# Revit family: Toilet_Elongated-American_Standard-Studio_S-2548A100.020
name_source: partatom
category: Plumbing Fixtures
units: mm (PartAtom-declared; Revit-internal decimal feet)

## family parameters
Always vertical = No
Cut with Voids When Loaded = No
OmniClass Number = 23.45.05.21.11
OmniClass Title = Water Closets
Part Type = Normal
Room Calculation Point = No
Round Connector Dimension = Use Diameter
Shared = Yes
Work Plane-Based = Yes

## types (1)
- 2548A100.020
    ADA Compliant = Yes
    Assembly Code = D2010110
    Bowl Shape = Elongated
    CEC Compliant = Yes
    CW Connection = Yes
    CWFU = 5
    CalGreen Compliant = Yes
    Cold Water Connection Diameter = 1/2"
    Cold Water Connection Height = 5 1/2"
    Cold Water Connection Radius = 1/4"
    Cold Water Connection Width = 10"
    Compliance Certifications = Meets or Exceeds ASME A112.19.2/CSA B45.1 For Vitreous China Fixtures , US EPA WaterSense® Specification for UHETs
    Default Elevation = 0"
    Description = Studio® S One-Piece 1.0 gpf/3.8 Lpf Chair Height Elongated Toilet With Seat
    Finish = Vitreous China-American Standard-020-White
    Flush Rate = 1.0 gpf (3.8 Lpf)
    HW Connection = No
    HWFU = 0
    Height = 18 1/2"
    Inlet Supply Position 1 = Yes
    Inlet Supply Position 2 - Behind the Toilet = No
    Installation Type = Floor Mounted
    Length = 31 1/8"
    Manufacturer = American Standard
    Material = Vitreous China-American Standard-020-White
    Model = 2548A100.020
    Price = Prices may vary. Please consult Manufacturer Representative for most up-to-date price list.
    Product Documentation Link = https://americanstandard.box.com
    Product Page URL = https://www.americanstandard-us.com
    Revised Date = 03/16/22
    URL = https://www.americanstandard-us.com
    Vent Connection = No
    WFU = 5
    Warranty Information = Lifetime warranty on chinaware, 5-year warranty on all mechanical parts, 1-year warranty on seat
    Waste Connection = Yes
    Waste Connection Diameter = 2"
    Waste Connection Radius = 1"
    Waste Connection Width = 12"
    Width = 16 3/8"

## geometry (parser evidence)
native form markers: Sweep x2
no freeform markers — native parametric forms only
